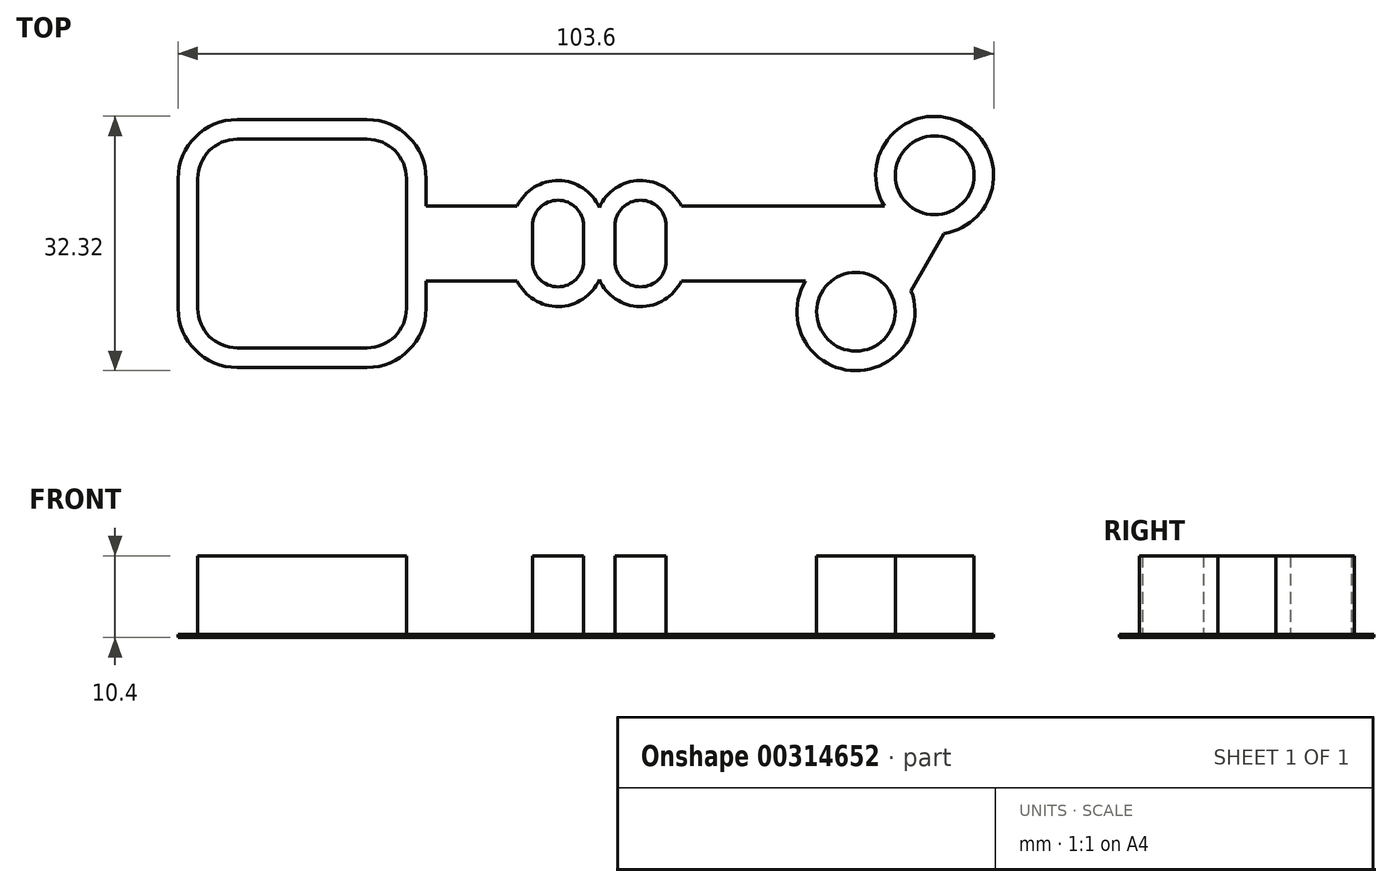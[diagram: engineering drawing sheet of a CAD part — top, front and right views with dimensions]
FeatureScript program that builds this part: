
annotation { "Feature Type Name" : "Feature", "Feature Type Description" : "" }
export const myFeature = defineFeature(function(context is Context, id is Id, definition is map)
    precondition{}
    {
        {
            var Q0;
            Q0=qCreatedBy(makeId("Top.planeOp"),FACE);
            var sketch = newSketch(context, id + "F0", { "sketchPlane" : qUnion([Q0])});
            skLineSegment(sketch, "E0.bottom", {"start": v(8.25, 13.25) * mm, "end": v(-8.25, 13.25) * mm});
            skLineSegment(sketch, "E0.top", {"start": v(8.25, -13.25) * mm, "end": v(-8.25, -13.25) * mm});
            skLineSegment(sketch, "E0.left", {"start": v(13.25, 8.25) * mm, "end": v(13.25, 2.25) * mm});
            skLineSegment(sketch, "E0.right", {"start": v(-13.25, 8.25) * mm, "end": v(-13.25, -8.25) * mm});
            skPoint(sketch, "E0.middle", {"position": v(0, 0) * mm});
            skPoint(sketch, "E1.visualSharp", {"position": v(-13.25, 13.25) * mm});
            skArc(sketch, "E1.filletArc", {"start": v(-8.25, 13.25) * mm, "mid": v(-11.79, 11.79) * mm, "end": v(-13.25, 8.25) * mm});
            skPoint(sketch, "E2.visualSharp", {"position": v(13.25, 13.25) * mm});
            skArc(sketch, "E2.filletArc", {"start": v(13.25, 8.25) * mm, "mid": v(11.79, 11.79) * mm, "end": v(8.25, 13.25) * mm});
            skPoint(sketch, "E3.visualSharp", {"position": v(13.25, -13.25) * mm});
            skArc(sketch, "E3.filletArc", {"start": v(8.25, -13.25) * mm, "mid": v(11.79, -11.79) * mm, "end": v(13.25, -8.25) * mm});
            skPoint(sketch, "E4.visualSharp", {"position": v(-13.25, -13.25) * mm});
            skArc(sketch, "E4.filletArc", {"start": v(-13.25, -8.25) * mm, "mid": v(-11.79, -11.79) * mm, "end": v(-8.25, -13.25) * mm});
            skCircle(sketch, "E5", {"center": v(0, 0) * mm, "radius": 4.5 * mm});
            skLineSegment(sketch, "E6", {"start": v(-4.5, 13.25) * mm, "end": v(-4.5, -13.25) * mm});
            skLineSegment(sketch, "E7", {"start": v(4.5, 13.25) * mm, "end": v(4.5, -13.25) * mm});
            skLineSegment(sketch, "E8", {"start": v(-13.25, 4.5) * mm, "end": v(13.25, 4.5) * mm});
            skLineSegment(sketch, "E9", {"start": v(-13.25, -4.5) * mm, "end": v(13.25, -4.5) * mm});
            skLineSegment(sketch, "E10", {"start": v(-69.25, 0) * mm, "end": v(-69.25, 0) * mm});
            skPoint(sketch, "E10.endSnap0", {"position": v(13.25, 0) * mm});
            skLineSegment(sketch, "E11", {"start": v(13.25, 2.25) * mm, "end": v(29.25, 2.25) * mm});
            skLineSegment(sketch, "E12.bottom", {"start": v(29.25, 2.25) * mm, "end": v(35.75, 2.25) * mm});
            skLineSegment(sketch, "E12.top", {"start": v(29.25, -2.25) * mm, "end": v(35.75, -2.25) * mm});
            skLineSegment(sketch, "E12.left", {"start": v(29.25, 2.25) * mm, "end": v(29.25, -2.25) * mm});
            skLineSegment(sketch, "E12.right", {"start": v(35.75, 2.25) * mm, "end": v(35.75, -2.25) * mm});
            skLineSegment(sketch, "E13", {"start": v(37.75, 52.13) * mm, "end": v(37.75, -65.63) * mm, "construction": true});
            skLineSegment(sketch, "E14", {"start": v(-69.25, 0) * mm, "end": v(131.45, 0) * mm, "construction": true});
            skLineSegment(sketch, "E15.MirrorCS", {"start": v(13.25, -2.25) * mm, "end": v(13.25, -2.25) * mm});
            skLineSegment(sketch, "E16.MirrorCS", {"start": v(46.25, -2.25) * mm, "end": v(39.75, -2.25) * mm});
            skLineSegment(sketch, "E17.MirrorCS", {"start": v(46.25, 2.25) * mm, "end": v(46.25, -2.25) * mm});
            skLineSegment(sketch, "E18.MirrorCS", {"start": v(39.75, 2.25) * mm, "end": v(39.75, -2.25) * mm});
            skLineSegment(sketch, "E19.MirrorCS", {"start": v(46.25, 2.25) * mm, "end": v(39.75, 2.25) * mm});
            skLineSegment(sketch, "E20", {"start": v(35.75, 2.25) * mm, "end": v(39.75, 2.25) * mm});
            skLineSegment(sketch, "E21", {"start": v(35.75, -2.25) * mm, "end": v(39.75, -2.25) * mm});
            skArc(sketch, "E22", {"start": v(29.25, 2.25) * mm, "mid": v(32.5, 5.5) * mm, "end": v(35.75, 2.25) * mm});
            skArc(sketch, "E23.MirrorCS", {"start": v(29.25, -2.25) * mm, "mid": v(32.5, -5.5) * mm, "end": v(35.75, -2.25) * mm});
            skArc(sketch, "E24.MirrorCS", {"start": v(46.25, 2.25) * mm, "mid": v(43, 5.5) * mm, "end": v(39.75, 2.25) * mm});
            skArc(sketch, "E25.MirrorCS", {"start": v(46.25, -2.25) * mm, "mid": v(43, -5.5) * mm, "end": v(39.75, -2.25) * mm});
            skLineSegment(sketch, "E26", {"start": v(46.25, 2.25) * mm, "end": v(74.05, 2.25) * mm});
            skLineSegment(sketch, "E27", {"start": v(70.35, -8.66) * mm, "end": v(80.35, 8.66) * mm, "construction": true});
            skPoint(sketch, "E28", {"position": v(75.35, 0) * mm});
            skLineSegment(sketch, "E29", {"start": v(76.17, 5.92) * mm, "end": v(74.05, 2.25) * mm});
            skLineSegment(sketch, "E30.MirrorCS", {"start": v(80.06, 3.67) * mm, "end": v(74.53, -5.92) * mm});
            skPoint(sketch, "E31", {"position": v(72.75, 0) * mm});
            skLineSegment(sketch, "E32.MirrorCS", {"start": v(46.25, -2.25) * mm, "end": v(71.45, -2.25) * mm});
            skPoint(sketch, "E33.orphan", {"position": v(72.75, -2.25) * mm});
            skPoint(sketch, "E34.orphan", {"position": v(72.75, 2.25) * mm});
            skLineSegment(sketch, "E35", {"start": v(13.25, 2.25) * mm, "end": v(13.25, -2.25) * mm});
            skLineSegment(sketch, "E36", {"start": v(13.25, -2.25) * mm, "end": v(29.25, -2.25) * mm});
            skLineSegment(sketch, "E37", {"start": v(13.25, -2.25) * mm, "end": v(13.25, -8.25) * mm});
            skLineSegment(sketch, "E38", {"start": v(71.45, -2.25) * mm, "end": v(71.45, -2.25) * mm});
            skLineSegment(sketch, "E39", {"start": v(74.05, 2.25) * mm, "end": v(71.45, -2.25) * mm});
            skLineSegment(sketch, "E40", {"start": v(71.45, -2.25) * mm, "end": v(70.63, -3.67) * mm});
            skArc(sketch, "E41", {"start": v(70.63, -3.67) * mm, "mid": v(67.85, -13) * mm, "end": v(74.53, -5.92) * mm});
            skArc(sketch, "E42", {"start": v(74.53, -5.92) * mm, "mid": v(72.85, -4.33) * mm, "end": v(70.63, -3.67) * mm});
            skArc(sketch, "E43", {"start": v(76.17, 5.92) * mm, "mid": v(77.85, 4.33) * mm, "end": v(80.06, 3.67) * mm});
            skArc(sketch, "E44", {"start": v(80.06, 3.67) * mm, "mid": v(82.85, 13) * mm, "end": v(76.17, 5.92) * mm});
            skLineSegment(sketch, "E45.0", {"start": v(46.25, -4.25) * mm, "end": v(71.45, -4.25) * mm});
            skLineSegment(sketch, "E46.0", {"start": v(15.75, 8.25) * mm, "end": v(15.75, 4.75) * mm});
            skLineSegment(sketch, "E46.1", {"start": v(15.75, 4.75) * mm, "end": v(27.32, 4.75) * mm});
            skArc(sketch, "E46.2", {"start": v(27.32, 4.75) * mm, "mid": v(32.59, 8) * mm, "end": v(37.75, 4.6) * mm});
            skArc(sketch, "E46.3", {"start": v(48.18, 4.75) * mm, "mid": v(42.91, 8) * mm, "end": v(37.75, 4.6) * mm});
            skLineSegment(sketch, "E46.4", {"start": v(48.18, 4.75) * mm, "end": v(73.95, 4.75) * mm});
            skArc(sketch, "E46.5", {"start": v(15.75, 8.25) * mm, "mid": v(13.55, 13.55) * mm, "end": v(8.25, 15.75) * mm});
            skArc(sketch, "E46.6", {"start": v(81.56, 1.26) * mm, "mid": v(83.47, 15.48) * mm, "end": v(73.95, 4.75) * mm});
            skLineSegment(sketch, "E46.7", {"start": v(81.56, 1.26) * mm, "end": v(77.36, -6) * mm});
            skArc(sketch, "E46.8", {"start": v(63.95, -4.75) * mm, "mid": v(69.65, -16.13) * mm, "end": v(77.36, -6) * mm});
            skLineSegment(sketch, "E46.9", {"start": v(48.18, -4.75) * mm, "end": v(63.95, -4.75) * mm});
            skArc(sketch, "E46.10", {"start": v(-15.75, -8.25) * mm, "mid": v(-13.55, -13.55) * mm, "end": v(-8.25, -15.75) * mm});
            skLineSegment(sketch, "E46.11", {"start": v(-15.75, 8.25) * mm, "end": v(-15.75, -8.25) * mm});
            skArc(sketch, "E46.12", {"start": v(-8.25, 15.75) * mm, "mid": v(-13.55, 13.55) * mm, "end": v(-15.75, 8.25) * mm});
            skLineSegment(sketch, "E46.13", {"start": v(8.25, 15.75) * mm, "end": v(-8.25, 15.75) * mm});
            skLineSegment(sketch, "E46.14", {"start": v(8.25, -15.75) * mm, "end": v(-8.25, -15.75) * mm});
            skArc(sketch, "E46.15", {"start": v(8.25, -15.75) * mm, "mid": v(13.55, -13.55) * mm, "end": v(15.75, -8.25) * mm});
            skLineSegment(sketch, "E46.16", {"start": v(15.75, -4.75) * mm, "end": v(15.75, -8.25) * mm});
            skLineSegment(sketch, "E46.17", {"start": v(15.75, -4.75) * mm, "end": v(27.32, -4.75) * mm});
            skArc(sketch, "E46.18", {"start": v(27.32, -4.75) * mm, "mid": v(32.59, -8) * mm, "end": v(37.75, -4.6) * mm});
            skArc(sketch, "E46.19", {"start": v(48.18, -4.75) * mm, "mid": v(42.91, -8) * mm, "end": v(37.75, -4.6) * mm});
            skSolve(sketch);
        }
        {
            var Q0;
            {var subQ9=sQuery(id+"F0.wireOp",EDGE,"E1.filletArc");Q0=makeQuery(id+"F0.imprint","IMPRINT",FACE,{"disambiguationData":[TD([[makeQuery(id+"F0.imprint","IMPRINT",EDGE,{"derivedFrom":subQ9}),-1.0]])]});}
            var Q1;
            {var subQ7=sQuery(id+"F0.wireOp",EDGE,"E3.filletArc");Q1=makeQuery(id+"F0.imprint","IMPRINT",FACE,{"disambiguationData":[TD([[makeQuery(id+"F0.imprint","IMPRINT",EDGE,{"derivedFrom":subQ7}),1.0]])]});}
            var Q2;
            {var subQ8=sQuery(id+"F0.wireOp",EDGE,"E35");Q2=makeQuery(id+"F0.imprint","IMPRINT",FACE,{"disambiguationData":[TD([[makeQuery(id+"F0.imprint","IMPRINT",EDGE,{"derivedFrom":subQ8}),-1.0]])]});}
            var Q3;
            {var subQ5=sQuery(id+"F0.wireOp",EDGE,"E2.filletArc");Q3=makeQuery(id+"F0.imprint","IMPRINT",FACE,{"disambiguationData":[TD([[makeQuery(id+"F0.imprint","IMPRINT",EDGE,{"derivedFrom":subQ5}),1.0]])]});}
            var Q4;
            {var subQ2=sQuery(id+"F0.wireOp",EDGE,"E6");var subQ5=sQuery(id+"F0.wireOp",EDGE,"E0.bottom");var subQ8=makeQuery(id+"F0.imprint","INTERSECT",VERTEX,{"derivedFrom":[subQ5,subQ2]});Q4=makeQuery(id+"F0.imprint","IMPRINT",FACE,{"disambiguationData":[TD([[makeQuery(id+"F0.imprint","IMPRINT",EDGE,{"disambiguationData":[TD([[subQ8,1.0]])],"derivedFrom":subQ5}),1.0]])]});}
            var Q5;
            Q5=makeQuery(id+"F0.imprint","IMPRINT",FACE,{"disambiguationData":[TD([[makeQuery(id+"F0.imprint","IMPRINT",EDGE,{"derivedFrom":sQuery(id+"F0.wireOp",EDGE,"E11")}),-1.0]])]});
            var Q6;
            Q6=makeQuery(id+"F0.imprint","IMPRINT",FACE,{"disambiguationData":[TD([[makeQuery(id+"F0.imprint","IMPRINT",EDGE,{"derivedFrom":sQuery(id+"F0.wireOp",EDGE,"E12.bottom")}),-1.0]])]});
            var Q7;
            Q7=makeQuery(id+"F0.imprint","IMPRINT",FACE,{"disambiguationData":[TD([[makeQuery(id+"F0.imprint","IMPRINT",EDGE,{"derivedFrom":sQuery(id+"F0.wireOp",EDGE,"E12.bottom")}),1.0]])]});
            var Q8;
            Q8=makeQuery(id+"F0.imprint","IMPRINT",FACE,{"disambiguationData":[TD([[makeQuery(id+"F0.imprint","IMPRINT",EDGE,{"derivedFrom":sQuery(id+"F0.wireOp",EDGE,"E12.top")}),-1.0]])]});
            var Q9;
            Q9=makeQuery(id+"F0.imprint","IMPRINT",FACE,{"disambiguationData":[TD([[makeQuery(id+"F0.imprint","IMPRINT",EDGE,{"derivedFrom":sQuery(id+"F0.wireOp",EDGE,"E12.right")}),1.0]])]});
            var Q10;
            Q10=makeQuery(id+"F0.imprint","IMPRINT",FACE,{"disambiguationData":[TD([[makeQuery(id+"F0.imprint","IMPRINT",EDGE,{"derivedFrom":sQuery(id+"F0.wireOp",EDGE,"E19.MirrorCS")}),-1.0]])]});
            var Q11;
            Q11=makeQuery(id+"F0.imprint","IMPRINT",FACE,{"disambiguationData":[TD([[makeQuery(id+"F0.imprint","IMPRINT",EDGE,{"derivedFrom":sQuery(id+"F0.wireOp",EDGE,"E16.MirrorCS")}),-1.0]])]});
            var Q12;
            Q12=makeQuery(id+"F0.imprint","IMPRINT",FACE,{"disambiguationData":[TD([[makeQuery(id+"F0.imprint","IMPRINT",EDGE,{"derivedFrom":sQuery(id+"F0.wireOp",EDGE,"E16.MirrorCS")}),1.0]])]});
            var Q13;
            Q13=makeQuery(id+"F0.imprint","IMPRINT",FACE,{"disambiguationData":[TD([[makeQuery(id+"F0.imprint","IMPRINT",EDGE,{"derivedFrom":sQuery(id+"F0.wireOp",EDGE,"E17.MirrorCS")}),1.0]])]});
            var Q14;
            Q14=makeQuery(id+"F0.imprint","IMPRINT",FACE,{"disambiguationData":[TD([[makeQuery(id+"F0.imprint","IMPRINT",EDGE,{"derivedFrom":sQuery(id+"F0.wireOp",EDGE,"E43")}),1.0]])]});
            var Q15;
            Q15=makeQuery(id+"F0.imprint","IMPRINT",FACE,{"disambiguationData":[TD([[makeQuery(id+"F0.imprint","IMPRINT",EDGE,{"derivedFrom":sQuery(id+"F0.wireOp",EDGE,"E29")}),1.0]])]});
            var Q16;
            {var subQ0=sQuery(id+"F0.wireOp",EDGE,"E42");Q16=makeQuery(id+"F0.imprint","IMPRINT",FACE,{"disambiguationData":[TD([[makeQuery(id+"F0.imprint","IMPRINT",EDGE,{"derivedFrom":subQ0}),1.0]])]});}
            var Q17;
            {var subQ1=sQuery(id+"F0.wireOp",EDGE,"E0.top");var subQ5=sQuery(id+"F0.wireOp",EDGE,"E6");var subQ6=makeQuery(id+"F0.imprint","INTERSECT",VERTEX,{"derivedFrom":[subQ1,subQ5]});Q17=makeQuery(id+"F0.imprint","IMPRINT",FACE,{"disambiguationData":[TD([[makeQuery(id+"F0.imprint","IMPRINT",EDGE,{"disambiguationData":[TD([[subQ6,1.0]])],"derivedFrom":subQ1}),-1.0]])]});}
            var Q18;
            {var subQ0=sQuery(id+"F0.wireOp",EDGE,"E5");var subQ1=makeQuery(id+"F0.imprint","INTERSECT",VERTEX,{"derivedFrom":[subQ0,sQuery(id+"F0.wireOp",EDGE,"E8")]});Q18=makeQuery(id+"F0.imprint","IMPRINT",FACE,{"disambiguationData":[TD([[makeQuery(id+"F0.imprint","IMPRINT",EDGE,{"disambiguationData":[TD([[subQ1,1.0]])],"derivedFrom":subQ0}),1.0]])]});}
            var Q19;
            {var subQ5=sQuery(id+"F0.wireOp",EDGE,"E4.filletArc");Q19=makeQuery(id+"F0.imprint","IMPRINT",FACE,{"disambiguationData":[TD([[makeQuery(id+"F0.imprint","IMPRINT",EDGE,{"derivedFrom":subQ5}),1.0]])]});}
            var Q20;
            {var subQ0=sQuery(id+"F0.wireOp",EDGE,"E8");var subQ1=sQuery(id+"F0.wireOp",EDGE,"E0.right");var subQ2=makeQuery(id+"F0.imprint","INTERSECT",VERTEX,{"derivedFrom":[subQ1,subQ0]});Q20=makeQuery(id+"F0.imprint","IMPRINT",FACE,{"disambiguationData":[TD([[makeQuery(id+"F0.imprint","IMPRINT",EDGE,{"disambiguationData":[TD([[subQ2,-1.0]])],"derivedFrom":subQ1}),1.0]])]});}
            var Q21;
            {var subQ5=sQuery(id+"F0.wireOp",EDGE,"E1.filletArc");Q21=makeQuery(id+"F0.imprint","IMPRINT",FACE,{"disambiguationData":[TD([[makeQuery(id+"F0.imprint","IMPRINT",EDGE,{"derivedFrom":subQ5}),1.0]])]});}
            var Q22;
            {var subQ0=sQuery(id+"F0.wireOp",EDGE,"E8");var subQ1=sQuery(id+"F0.wireOp",EDGE,"E5");var subQ2=makeQuery(id+"F0.imprint","INTERSECT",VERTEX,{"derivedFrom":[subQ1,subQ0]});Q22=makeQuery(id+"F0.imprint","IMPRINT",FACE,{"disambiguationData":[TD([[makeQuery(id+"F0.imprint","IMPRINT",EDGE,{"disambiguationData":[TD([[subQ2,1.0]])],"derivedFrom":subQ1}),-1.0]])]});}
            var Q23;
            {var subQ0=sQuery(id+"F0.wireOp",EDGE,"E7");var subQ1=sQuery(id+"F0.wireOp",EDGE,"E5");var subQ2=makeQuery(id+"F0.imprint","INTERSECT",VERTEX,{"derivedFrom":[subQ1,subQ0]});Q23=makeQuery(id+"F0.imprint","IMPRINT",FACE,{"disambiguationData":[TD([[makeQuery(id+"F0.imprint","IMPRINT",EDGE,{"disambiguationData":[TD([[subQ2,1.0]])],"derivedFrom":subQ1}),-1.0]])]});}
            var Q24;
            {var subQ0=sQuery(id+"F0.wireOp",EDGE,"E6");var subQ1=sQuery(id+"F0.wireOp",EDGE,"E5");var subQ2=makeQuery(id+"F0.imprint","INTERSECT",VERTEX,{"derivedFrom":[subQ1,subQ0]});Q24=makeQuery(id+"F0.imprint","IMPRINT",FACE,{"disambiguationData":[TD([[makeQuery(id+"F0.imprint","IMPRINT",EDGE,{"disambiguationData":[TD([[subQ2,-1.0]])],"derivedFrom":subQ1}),-1.0]])]});}
            var Q25;
            {var subQ0=sQuery(id+"F0.wireOp",EDGE,"E8");var subQ1=sQuery(id+"F0.wireOp",EDGE,"E5");var subQ2=makeQuery(id+"F0.imprint","INTERSECT",VERTEX,{"derivedFrom":[subQ1,subQ0]});Q25=makeQuery(id+"F0.imprint","IMPRINT",FACE,{"disambiguationData":[TD([[makeQuery(id+"F0.imprint","IMPRINT",EDGE,{"disambiguationData":[TD([[subQ2,-1.0]])],"derivedFrom":subQ1}),-1.0]])]});}
            extrude(context, id + "F1", {"entities" : qUnion([Q0, Q1, Q2, Q3, Q4, Q5, Q6, Q7, Q8, Q9, Q10, Q11, Q12, Q13, Q14, Q15, Q16, Q17, Q18, Q19, Q20, Q21, Q22, Q23, Q24, Q25]), "depth" : 0.4 * mm});
        }
        {
            var Q0;
            Q0=makeQuery(id+"F1.opExtrude","CAP_FACE",FACE,{"disambiguationData":[OSD([sQuery(id+"F0.wireOp",EDGE,"E46.0"),sQuery(id+"F0.wireOp",EDGE,"E46.1"),sQuery(id+"F0.wireOp",EDGE,"E46.2"),sQuery(id+"F0.wireOp",EDGE,"E46.3"),sQuery(id+"F0.wireOp",EDGE,"E46.4"),sQuery(id+"F0.wireOp",EDGE,"E46.5"),sQuery(id+"F0.wireOp",EDGE,"E46.6"),sQuery(id+"F0.wireOp",EDGE,"E46.7"),sQuery(id+"F0.wireOp",EDGE,"E46.8"),sQuery(id+"F0.wireOp",EDGE,"E46.9"),sQuery(id+"F0.wireOp",EDGE,"E46.10"),sQuery(id+"F0.wireOp",EDGE,"E46.11"),sQuery(id+"F0.wireOp",EDGE,"E46.12"),sQuery(id+"F0.wireOp",EDGE,"E46.13"),sQuery(id+"F0.wireOp",EDGE,"E46.14"),sQuery(id+"F0.wireOp",EDGE,"E46.15"),sQuery(id+"F0.wireOp",EDGE,"E46.16"),sQuery(id+"F0.wireOp",EDGE,"E46.17"),sQuery(id+"F0.wireOp",EDGE,"E46.18"),sQuery(id+"F0.wireOp",EDGE,"E46.19")])],"isStart":false});
            var sketch = newSketch(context, id + "F2", { "sketchPlane" : qUnion([Q0])});
            skLineSegment(sketch, "E47.0", {"start": v(8.25, 13.25) * mm, "end": v(-8.25, 13.25) * mm});
            skLineSegment(sketch, "E47.1", {"start": v(8.25, -13.25) * mm, "end": v(-8.25, -13.25) * mm});
            skLineSegment(sketch, "E47.2", {"start": v(13.25, 8.25) * mm, "end": v(13.25, 2.25) * mm});
            skLineSegment(sketch, "E47.3", {"start": v(-13.25, 8.25) * mm, "end": v(-13.25, -8.25) * mm});
            skPoint(sketch, "E47.4", {"position": v(0, 0) * mm});
            skPoint(sketch, "E47.5", {"position": v(-13.25, 13.25) * mm});
            skArc(sketch, "E47.6", {"start": v(-8.25, 13.25) * mm, "mid": v(-11.79, 11.79) * mm, "end": v(-13.25, 8.25) * mm});
            skPoint(sketch, "E47.7", {"position": v(13.25, 13.25) * mm});
            skArc(sketch, "E47.8", {"start": v(13.25, 8.25) * mm, "mid": v(11.79, 11.79) * mm, "end": v(8.25, 13.25) * mm});
            skPoint(sketch, "E47.9", {"position": v(13.25, -13.25) * mm});
            skArc(sketch, "E47.10", {"start": v(8.25, -13.25) * mm, "mid": v(11.79, -11.79) * mm, "end": v(13.25, -8.25) * mm});
            skPoint(sketch, "E47.11", {"position": v(-13.25, -13.25) * mm});
            skArc(sketch, "E47.12", {"start": v(-13.25, -8.25) * mm, "mid": v(-11.79, -11.79) * mm, "end": v(-8.25, -13.25) * mm});
            skCircle(sketch, "E47.13", {"center": v(0, 0) * mm, "radius": 4.5 * mm});
            skLineSegment(sketch, "E47.14", {"start": v(-4.5, 13.25) * mm, "end": v(-4.5, -13.25) * mm});
            skLineSegment(sketch, "E47.15", {"start": v(4.5, 13.25) * mm, "end": v(4.5, -13.25) * mm});
            skLineSegment(sketch, "E47.16", {"start": v(-13.25, 4.5) * mm, "end": v(13.25, 4.5) * mm});
            skLineSegment(sketch, "E47.17", {"start": v(-13.25, -4.5) * mm, "end": v(13.25, -4.5) * mm});
            skPoint(sketch, "E47.19", {"position": v(13.25, 0) * mm});
            skLineSegment(sketch, "E47.20", {"start": v(13.25, 2.25) * mm, "end": v(29.25, 2.25) * mm});
            skLineSegment(sketch, "E47.21", {"start": v(29.25, 2.25) * mm, "end": v(35.75, 2.25) * mm});
            skLineSegment(sketch, "E47.22", {"start": v(29.25, -2.25) * mm, "end": v(35.75, -2.25) * mm});
            skLineSegment(sketch, "E47.23", {"start": v(29.25, 2.25) * mm, "end": v(29.25, -2.25) * mm});
            skLineSegment(sketch, "E47.24", {"start": v(35.75, 2.25) * mm, "end": v(35.75, -2.25) * mm});
            skPoint(sketch, "E47.27", {"position": v(13.25, -2.25) * mm});
            skLineSegment(sketch, "E47.28", {"start": v(46.25, -2.25) * mm, "end": v(39.75, -2.25) * mm});
            skLineSegment(sketch, "E47.29", {"start": v(46.25, 2.25) * mm, "end": v(46.25, -2.25) * mm});
            skLineSegment(sketch, "E47.30", {"start": v(39.75, 2.25) * mm, "end": v(39.75, -2.25) * mm});
            skLineSegment(sketch, "E47.31", {"start": v(46.25, 2.25) * mm, "end": v(39.75, 2.25) * mm});
            skLineSegment(sketch, "E47.32", {"start": v(35.75, 2.25) * mm, "end": v(39.75, 2.25) * mm});
            skLineSegment(sketch, "E47.33", {"start": v(35.75, -2.25) * mm, "end": v(39.75, -2.25) * mm});
            skArc(sketch, "E47.34", {"start": v(29.25, 2.25) * mm, "mid": v(32.5, 5.5) * mm, "end": v(35.75, 2.25) * mm});
            skArc(sketch, "E47.35", {"start": v(29.25, -2.25) * mm, "mid": v(32.5, -5.5) * mm, "end": v(35.75, -2.25) * mm});
            skArc(sketch, "E47.36", {"start": v(46.25, 2.25) * mm, "mid": v(43, 5.5) * mm, "end": v(39.75, 2.25) * mm});
            skArc(sketch, "E47.37", {"start": v(46.25, -2.25) * mm, "mid": v(43, -5.5) * mm, "end": v(39.75, -2.25) * mm});
            skLineSegment(sketch, "E47.38", {"start": v(46.25, 2.25) * mm, "end": v(74.05, 2.25) * mm});
            skLineSegment(sketch, "E47.39", {"start": v(70.35, -8.66) * mm, "end": v(80.35, 8.66) * mm});
            skPoint(sketch, "E47.40", {"position": v(75.35, 0) * mm});
            skLineSegment(sketch, "E47.41", {"start": v(76.17, 5.92) * mm, "end": v(74.05, 2.25) * mm});
            skLineSegment(sketch, "E47.42", {"start": v(80.06, 3.67) * mm, "end": v(74.53, -5.92) * mm});
            skPoint(sketch, "E47.43", {"position": v(72.75, 0) * mm});
            skLineSegment(sketch, "E47.44", {"start": v(46.25, -2.25) * mm, "end": v(71.45, -2.25) * mm});
            skPoint(sketch, "E47.45", {"position": v(72.75, -2.25) * mm});
            skPoint(sketch, "E47.46", {"position": v(72.75, 2.25) * mm});
            skLineSegment(sketch, "E47.47", {"start": v(13.25, 2.25) * mm, "end": v(13.25, -2.25) * mm});
            skLineSegment(sketch, "E47.48", {"start": v(13.25, -2.25) * mm, "end": v(29.25, -2.25) * mm});
            skLineSegment(sketch, "E47.49", {"start": v(13.25, -2.25) * mm, "end": v(13.25, -8.25) * mm});
            skPoint(sketch, "E47.50", {"position": v(71.45, -2.25) * mm});
            skLineSegment(sketch, "E47.51", {"start": v(74.05, 2.25) * mm, "end": v(71.45, -2.25) * mm});
            skLineSegment(sketch, "E47.52", {"start": v(71.45, -2.25) * mm, "end": v(70.63, -3.67) * mm});
            skArc(sketch, "E47.53", {"start": v(70.63, -3.67) * mm, "mid": v(67.85, -13) * mm, "end": v(74.53, -5.92) * mm});
            skArc(sketch, "E47.54", {"start": v(74.53, -5.92) * mm, "mid": v(72.85, -4.33) * mm, "end": v(70.63, -3.67) * mm});
            skArc(sketch, "E47.55", {"start": v(76.17, 5.92) * mm, "mid": v(77.85, 4.33) * mm, "end": v(80.06, 3.67) * mm});
            skArc(sketch, "E47.56", {"start": v(80.06, 3.67) * mm, "mid": v(82.85, 13) * mm, "end": v(76.17, 5.92) * mm});
            skLineSegment(sketch, "E47.58", {"start": v(15.75, 8.25) * mm, "end": v(15.75, 4.75) * mm});
            skLineSegment(sketch, "E47.59", {"start": v(15.75, 4.75) * mm, "end": v(27.32, 4.75) * mm});
            skArc(sketch, "E47.60", {"start": v(27.32, 4.75) * mm, "mid": v(32.59, 8) * mm, "end": v(37.75, 4.6) * mm});
            skArc(sketch, "E47.61", {"start": v(48.18, 4.75) * mm, "mid": v(42.91, 8) * mm, "end": v(37.75, 4.6) * mm});
            skLineSegment(sketch, "E47.62", {"start": v(48.18, 4.75) * mm, "end": v(73.95, 4.75) * mm});
            skArc(sketch, "E47.63", {"start": v(15.75, 8.25) * mm, "mid": v(13.55, 13.55) * mm, "end": v(8.25, 15.75) * mm});
            skArc(sketch, "E47.64", {"start": v(81.56, 1.26) * mm, "mid": v(83.47, 15.48) * mm, "end": v(73.95, 4.75) * mm});
            skLineSegment(sketch, "E47.65", {"start": v(81.56, 1.26) * mm, "end": v(77.36, -6) * mm});
            skArc(sketch, "E47.66", {"start": v(63.95, -4.75) * mm, "mid": v(69.65, -16.13) * mm, "end": v(77.36, -6) * mm});
            skLineSegment(sketch, "E47.67", {"start": v(48.18, -4.75) * mm, "end": v(63.95, -4.75) * mm});
            skArc(sketch, "E47.68", {"start": v(-15.75, -8.25) * mm, "mid": v(-13.55, -13.55) * mm, "end": v(-8.25, -15.75) * mm});
            skLineSegment(sketch, "E47.69", {"start": v(-15.75, 8.25) * mm, "end": v(-15.75, -8.25) * mm});
            skArc(sketch, "E47.70", {"start": v(-8.25, 15.75) * mm, "mid": v(-13.55, 13.55) * mm, "end": v(-15.75, 8.25) * mm});
            skLineSegment(sketch, "E47.71", {"start": v(8.25, 15.75) * mm, "end": v(-8.25, 15.75) * mm});
            skLineSegment(sketch, "E47.72", {"start": v(8.25, -15.75) * mm, "end": v(-8.25, -15.75) * mm});
            skArc(sketch, "E47.73", {"start": v(8.25, -15.75) * mm, "mid": v(13.55, -13.55) * mm, "end": v(15.75, -8.25) * mm});
            skLineSegment(sketch, "E47.74", {"start": v(15.75, -4.75) * mm, "end": v(15.75, -8.25) * mm});
            skLineSegment(sketch, "E47.75", {"start": v(15.75, -4.75) * mm, "end": v(27.32, -4.75) * mm});
            skArc(sketch, "E47.76", {"start": v(27.32, -4.75) * mm, "mid": v(32.59, -8) * mm, "end": v(37.75, -4.6) * mm});
            skArc(sketch, "E47.77", {"start": v(48.18, -4.75) * mm, "mid": v(42.91, -8) * mm, "end": v(37.75, -4.6) * mm});
            skSolve(sketch);
        }
        {
            var Q0;
            {var subQ5=sQuery(id+"F2.wireOp",EDGE,"E47.6");Q0=makeQuery(id+"F2.imprint","IMPRINT",FACE,{"disambiguationData":[TD([[makeQuery(id+"F2.imprint","IMPRINT",EDGE,{"derivedFrom":subQ5}),1.0]])]});}
            var Q1;
            {var subQ2=sQuery(id+"F2.wireOp",EDGE,"E47.14");var subQ5=sQuery(id+"F2.wireOp",EDGE,"E47.0");var subQ8=makeQuery(id+"F2.imprint","INTERSECT",VERTEX,{"derivedFrom":[subQ5,subQ2]});Q1=makeQuery(id+"F2.imprint","IMPRINT",FACE,{"disambiguationData":[TD([[makeQuery(id+"F2.imprint","IMPRINT",EDGE,{"disambiguationData":[TD([[subQ8,1.0]])],"derivedFrom":subQ5}),1.0]])]});}
            var Q2;
            {var subQ5=sQuery(id+"F2.wireOp",EDGE,"E47.8");Q2=makeQuery(id+"F2.imprint","IMPRINT",FACE,{"disambiguationData":[TD([[makeQuery(id+"F2.imprint","IMPRINT",EDGE,{"derivedFrom":subQ5}),1.0]])]});}
            var Q3;
            {var subQ10=sQuery(id+"F2.wireOp",EDGE,"E47.47");Q3=makeQuery(id+"F2.imprint","IMPRINT",FACE,{"disambiguationData":[TD([[makeQuery(id+"F2.imprint","IMPRINT",EDGE,{"derivedFrom":subQ10}),-1.0]])]});}
            var Q4;
            {var subQ1=sQuery(id+"F2.wireOp",EDGE,"E47.1");var subQ5=sQuery(id+"F2.wireOp",EDGE,"E47.14");var subQ6=makeQuery(id+"F2.imprint","INTERSECT",VERTEX,{"derivedFrom":[subQ1,subQ5]});Q4=makeQuery(id+"F2.imprint","IMPRINT",FACE,{"disambiguationData":[TD([[makeQuery(id+"F2.imprint","IMPRINT",EDGE,{"disambiguationData":[TD([[subQ6,1.0]])],"derivedFrom":subQ1}),-1.0]])]});}
            var Q5;
            {var subQ5=sQuery(id+"F2.wireOp",EDGE,"E47.12");Q5=makeQuery(id+"F2.imprint","IMPRINT",FACE,{"disambiguationData":[TD([[makeQuery(id+"F2.imprint","IMPRINT",EDGE,{"derivedFrom":subQ5}),1.0]])]});}
            var Q6;
            {var subQ0=sQuery(id+"F2.wireOp",EDGE,"E47.16");var subQ1=sQuery(id+"F2.wireOp",EDGE,"E47.3");var subQ2=makeQuery(id+"F2.imprint","INTERSECT",VERTEX,{"derivedFrom":[subQ1,subQ0]});Q6=makeQuery(id+"F2.imprint","IMPRINT",FACE,{"disambiguationData":[TD([[makeQuery(id+"F2.imprint","IMPRINT",EDGE,{"disambiguationData":[TD([[subQ2,-1.0]])],"derivedFrom":subQ1}),1.0]])]});}
            var Q7;
            {var subQ0=sQuery(id+"F2.wireOp",EDGE,"E47.13");var subQ1=makeQuery(id+"F2.imprint","INTERSECT",VERTEX,{"derivedFrom":[subQ0,sQuery(id+"F2.wireOp",EDGE,"E47.16")]});Q7=makeQuery(id+"F2.imprint","IMPRINT",FACE,{"disambiguationData":[TD([[makeQuery(id+"F2.imprint","IMPRINT",EDGE,{"disambiguationData":[TD([[subQ1,1.0]])],"derivedFrom":subQ0}),1.0]])]});}
            var Q8;
            {var subQ0=sQuery(id+"F2.wireOp",EDGE,"E47.16");var subQ1=sQuery(id+"F2.wireOp",EDGE,"E47.13");var subQ2=makeQuery(id+"F2.imprint","INTERSECT",VERTEX,{"derivedFrom":[subQ1,subQ0]});Q8=makeQuery(id+"F2.imprint","IMPRINT",FACE,{"disambiguationData":[TD([[makeQuery(id+"F2.imprint","IMPRINT",EDGE,{"disambiguationData":[TD([[subQ2,1.0]])],"derivedFrom":subQ1}),-1.0]])]});}
            var Q9;
            {var subQ0=sQuery(id+"F2.wireOp",EDGE,"E47.16");var subQ1=sQuery(id+"F2.wireOp",EDGE,"E47.13");var subQ2=makeQuery(id+"F2.imprint","INTERSECT",VERTEX,{"derivedFrom":[subQ1,subQ0]});Q9=makeQuery(id+"F2.imprint","IMPRINT",FACE,{"disambiguationData":[TD([[makeQuery(id+"F2.imprint","IMPRINT",EDGE,{"disambiguationData":[TD([[subQ2,-1.0]])],"derivedFrom":subQ1}),-1.0]])]});}
            var Q10;
            {var subQ0=sQuery(id+"F2.wireOp",EDGE,"E47.14");var subQ1=sQuery(id+"F2.wireOp",EDGE,"E47.13");var subQ2=makeQuery(id+"F2.imprint","INTERSECT",VERTEX,{"derivedFrom":[subQ1,subQ0]});Q10=makeQuery(id+"F2.imprint","IMPRINT",FACE,{"disambiguationData":[TD([[makeQuery(id+"F2.imprint","IMPRINT",EDGE,{"disambiguationData":[TD([[subQ2,-1.0]])],"derivedFrom":subQ1}),-1.0]])]});}
            var Q11;
            {var subQ0=sQuery(id+"F2.wireOp",EDGE,"E47.15");var subQ1=sQuery(id+"F2.wireOp",EDGE,"E47.13");var subQ2=makeQuery(id+"F2.imprint","INTERSECT",VERTEX,{"derivedFrom":[subQ1,subQ0]});Q11=makeQuery(id+"F2.imprint","IMPRINT",FACE,{"disambiguationData":[TD([[makeQuery(id+"F2.imprint","IMPRINT",EDGE,{"disambiguationData":[TD([[subQ2,1.0]])],"derivedFrom":subQ1}),-1.0]])]});}
            var Q12;
            {var subQ7=sQuery(id+"F2.wireOp",EDGE,"E47.10");Q12=makeQuery(id+"F2.imprint","IMPRINT",FACE,{"disambiguationData":[TD([[makeQuery(id+"F2.imprint","IMPRINT",EDGE,{"derivedFrom":subQ7}),1.0]])]});}
            var Q13;
            Q13=makeQuery(id+"F2.imprint","IMPRINT",FACE,{"disambiguationData":[TD([[makeQuery(id+"F2.imprint","IMPRINT",EDGE,{"derivedFrom":sQuery(id+"F2.wireOp",EDGE,"E47.21")}),1.0]])]});
            var Q14;
            Q14=makeQuery(id+"F2.imprint","IMPRINT",FACE,{"disambiguationData":[TD([[makeQuery(id+"F2.imprint","IMPRINT",EDGE,{"derivedFrom":sQuery(id+"F2.wireOp",EDGE,"E47.21")}),-1.0]])]});
            var Q15;
            Q15=makeQuery(id+"F2.imprint","IMPRINT",FACE,{"disambiguationData":[TD([[makeQuery(id+"F2.imprint","IMPRINT",EDGE,{"derivedFrom":sQuery(id+"F2.wireOp",EDGE,"E47.22")}),-1.0]])]});
            var Q16;
            Q16=makeQuery(id+"F2.imprint","IMPRINT",FACE,{"disambiguationData":[TD([[makeQuery(id+"F2.imprint","IMPRINT",EDGE,{"derivedFrom":sQuery(id+"F2.wireOp",EDGE,"E47.31")}),-1.0]])]});
            var Q17;
            Q17=makeQuery(id+"F2.imprint","IMPRINT",FACE,{"disambiguationData":[TD([[makeQuery(id+"F2.imprint","IMPRINT",EDGE,{"derivedFrom":sQuery(id+"F2.wireOp",EDGE,"E47.28")}),-1.0]])]});
            var Q18;
            Q18=makeQuery(id+"F2.imprint","IMPRINT",FACE,{"disambiguationData":[TD([[makeQuery(id+"F2.imprint","IMPRINT",EDGE,{"derivedFrom":sQuery(id+"F2.wireOp",EDGE,"E47.28")}),1.0]])]});
            var Q19;
            {var subQ0=sQuery(id+"F2.wireOp",EDGE,"E47.53");Q19=makeQuery(id+"F2.imprint","IMPRINT",FACE,{"disambiguationData":[TD([[makeQuery(id+"F2.imprint","IMPRINT",EDGE,{"derivedFrom":subQ0}),1.0]])]});}
            var Q20;
            {var subQ0=sQuery(id+"F2.wireOp",EDGE,"E47.56");Q20=makeQuery(id+"F2.imprint","IMPRINT",FACE,{"disambiguationData":[TD([[makeQuery(id+"F2.imprint","IMPRINT",EDGE,{"derivedFrom":subQ0}),1.0]])]});}
            extrude(context, id + "F3", {"entities" : qUnion([Q0, Q1, Q2, Q3, Q4, Q5, Q6, Q7, Q8, Q9, Q10, Q11, Q12, Q13, Q14, Q15, Q16, Q17, Q18, Q19, Q20]), "operationType" : NewBodyOperationType.ADD, "depth" : 10 * mm});
        }
        {
            var Q0;
            Q0=makeQuery(id+"F3.opExtrude","CAP_FACE",FACE,{"disambiguationData":[OSD([sQuery(id+"F2.wireOp",EDGE,"E47.0"),sQuery(id+"F2.wireOp",EDGE,"E47.1"),sQuery(id+"F2.wireOp",EDGE,"E47.2"),sQuery(id+"F2.wireOp",EDGE,"E47.3"),sQuery(id+"F2.wireOp",EDGE,"E47.6"),sQuery(id+"F2.wireOp",EDGE,"E47.8"),sQuery(id+"F2.wireOp",EDGE,"E47.10"),sQuery(id+"F2.wireOp",EDGE,"E47.12"),sQuery(id+"F2.wireOp",EDGE,"E47.47"),sQuery(id+"F2.wireOp",EDGE,"E47.49")])],"isStart":false});
            var sketch = newSketch(context, id + "F4", { "sketchPlane" : qUnion([Q0])});
            skLineSegment(sketch, "E48.0", {"start": v(8.25, 13.25) * mm, "end": v(-8.25, 13.25) * mm});
            skLineSegment(sketch, "E48.1", {"start": v(8.25, -13.25) * mm, "end": v(-8.25, -13.25) * mm});
            skLineSegment(sketch, "E48.2", {"start": v(13.25, 8.25) * mm, "end": v(13.25, 2.25) * mm});
            skLineSegment(sketch, "E48.3", {"start": v(-13.25, 8.25) * mm, "end": v(-13.25, -8.25) * mm});
            skPoint(sketch, "E48.4", {"position": v(0, 0) * mm});
            skPoint(sketch, "E48.5", {"position": v(-13.25, 13.25) * mm});
            skArc(sketch, "E48.6", {"start": v(-8.25, 13.25) * mm, "mid": v(-11.79, 11.79) * mm, "end": v(-13.25, 8.25) * mm});
            skPoint(sketch, "E48.7", {"position": v(13.25, 13.25) * mm});
            skArc(sketch, "E48.8", {"start": v(13.25, 8.25) * mm, "mid": v(11.79, 11.79) * mm, "end": v(8.25, 13.25) * mm});
            skPoint(sketch, "E48.9", {"position": v(13.25, -13.25) * mm});
            skArc(sketch, "E48.10", {"start": v(8.25, -13.25) * mm, "mid": v(11.79, -11.79) * mm, "end": v(13.25, -8.25) * mm});
            skPoint(sketch, "E48.11", {"position": v(-13.25, -13.25) * mm});
            skArc(sketch, "E48.12", {"start": v(-13.25, -8.25) * mm, "mid": v(-11.79, -11.79) * mm, "end": v(-8.25, -13.25) * mm});
            skCircle(sketch, "E48.13", {"center": v(0, 0) * mm, "radius": 4.5 * mm});
            skLineSegment(sketch, "E48.14", {"start": v(-4.5, 13.25) * mm, "end": v(-4.5, -13.25) * mm});
            skLineSegment(sketch, "E48.15", {"start": v(4.5, 13.25) * mm, "end": v(4.5, -13.25) * mm});
            skLineSegment(sketch, "E48.16", {"start": v(-13.25, 4.5) * mm, "end": v(13.25, 4.5) * mm});
            skLineSegment(sketch, "E48.17", {"start": v(-13.25, -4.5) * mm, "end": v(13.25, -4.5) * mm});
            skPoint(sketch, "E48.18", {"position": v(-69.25, 0) * mm});
            skPoint(sketch, "E48.19", {"position": v(13.25, 0) * mm});
            skLineSegment(sketch, "E48.20", {"start": v(13.25, 2.25) * mm, "end": v(29.25, 2.25) * mm});
            skLineSegment(sketch, "E48.25", {"start": v(37.75, 52.13) * mm, "end": v(37.75, -65.63) * mm});
            skLineSegment(sketch, "E48.26", {"start": v(-69.25, 0) * mm, "end": v(131.45, 0) * mm});
            skPoint(sketch, "E48.27", {"position": v(13.25, -2.25) * mm});
            skLineSegment(sketch, "E48.47", {"start": v(13.25, 2.25) * mm, "end": v(13.25, -2.25) * mm});
            skLineSegment(sketch, "E48.48", {"start": v(13.25, -2.25) * mm, "end": v(29.25, -2.25) * mm});
            skLineSegment(sketch, "E48.49", {"start": v(13.25, -2.25) * mm, "end": v(13.25, -8.25) * mm});
            skArc(sketch, "E48.63", {"start": v(15.75, 8.25) * mm, "mid": v(13.55, 13.55) * mm, "end": v(8.25, 15.75) * mm});
            skArc(sketch, "E48.68", {"start": v(-15.75, -8.25) * mm, "mid": v(-13.55, -13.55) * mm, "end": v(-8.25, -15.75) * mm});
            skLineSegment(sketch, "E48.69", {"start": v(-15.75, 8.25) * mm, "end": v(-15.75, -8.25) * mm});
            skArc(sketch, "E48.70", {"start": v(-8.25, 15.75) * mm, "mid": v(-13.55, 13.55) * mm, "end": v(-15.75, 8.25) * mm});
            skLineSegment(sketch, "E48.71", {"start": v(8.25, 15.75) * mm, "end": v(-8.25, 15.75) * mm});
            skLineSegment(sketch, "E48.72", {"start": v(8.25, -15.75) * mm, "end": v(-8.25, -15.75) * mm});
            skArc(sketch, "E48.73", {"start": v(8.25, -15.75) * mm, "mid": v(13.55, -13.55) * mm, "end": v(15.75, -8.25) * mm});
            skSolve(sketch);
        }
        {
            var Q0;
            Q0=sQuery(id+"F4.wireOp",EDGE,"E48.13");
            extrude(context, id + "F5", {"bodyType" : ToolBodyType.SURFACE, "surfaceEntities" : qUnion([Q0]), "depth" : 25 * mm});
        }
    });
